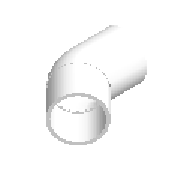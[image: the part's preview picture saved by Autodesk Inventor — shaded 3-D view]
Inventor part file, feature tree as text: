
AUTODESK INVENTOR PART (.ipt)
format: ipt  version: 2023 (Build 270158000, 158)  size: 257,024 bytes
history: native  units: mm (DEFAULTED — no unit token found)
features: revolve x6, other x6, sketch x3
ambient origin geometry x8: Origin, YZ Plane, XZ Plane, XY Plane, X Axis, Y Axis, Z Axis, Center Point
bodies: Solid1 (feature_tree)
feature tree (15):
  sketch  "Sketch1"  dims[d0=26.0mm d1=9.5mm]
  revolve  "Revolution1"  [1 undecoded]
  revolve  "Revolution2"  [1 undecoded]
  revolve  "Revolution3"  [1 undecoded]
  revolve  "Revolution4"  Angle=135.0deg
  sketch  "Sketch2"  dims[d2=40.0mm d3=3.0mm]
  revolve  "Revolution5"  Angle=90.0deg
  revolve  "Revolution6"  Angle=90.0deg
  other  "Work Point1"
  other  "Work Point2"
  other  "Work Axis1"
  other  "Work Point3"
  other  "Work Axis2"
  other  "Work Point4"
  sketch  "Sketch3"  dims[d4=3.0mm d5=40.0mm d6=135.0deg d139=90.0deg d140=90.0deg d7=26.0mm d8=9.5mm d9=1.615mm d10=1.615mm d11=38.0mm d203=7.845255mm d12=38.0mm d205=7.845255mm d13=38.0mm d14=46.0mm d15=0.01mm d16=45.0deg d17=2.0mm d18=80.0mm d19=45.0deg]
note: 3 required parameter values undecoded (feature->parameter linkage not recoverable at this tier; creation-order binding heuristic only, values carry confidence <= 0.55)
